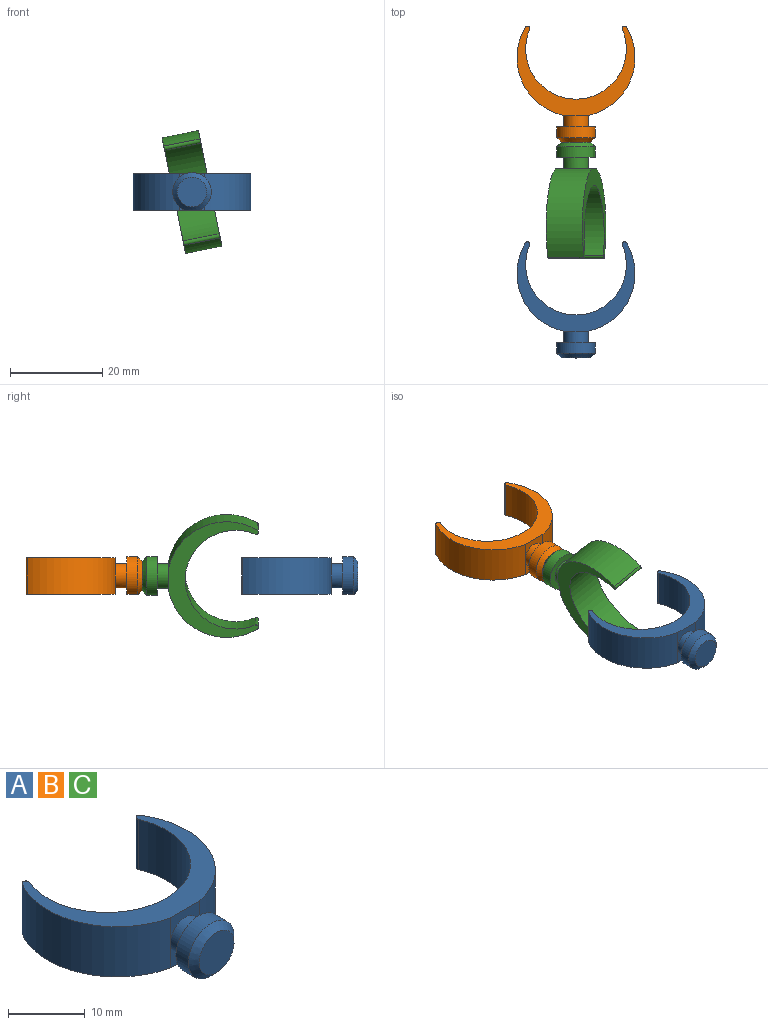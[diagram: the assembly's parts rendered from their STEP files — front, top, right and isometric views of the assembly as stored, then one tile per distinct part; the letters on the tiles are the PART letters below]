
ASSEMBLY  parts=3 mates=2
PART A: 15 faces, bbox 25.5x25.1x8.4 mm
  f0: cylinder r=2.7mm len=5.4mm, axis (0,1,0), area 42.4mm2, adj f1,f5,f6
  f1: plane 8.4x8.2mm, normal (0,1,0), area 32.2mm2, adj f0,f2,f12
  f2: cylinder r=4.2mm len=8.4mm, axis (0,1,0), area 54.7mm2, adj f1,f4,f12
  f3: plane 6.4x6.4mm, normal (0,-1,0), area 32.2mm2, adj f4
  f4: cone r=4.2mm half-angle=45deg, axis (0,1,0), area 32.4mm2, adj f2,f3,f12
  f5: plane 5.4x4mm, normal (0,-1,0), area 10.1mm2, adj f0,f8,f9,f11
  f6: plane 5.4x4mm, normal (0,-1,0), area 10.1mm2, adj f0,f8,f9,f10
  f7: cylinder r=10.9mm len=21.8mm, axis (0,0,-1), area 343.6mm2, adj f10,f11,f13,f14
  f8: cylinder r=12.77mm len=19.09mm, axis (0,0,-1), area 194.3mm2, adj f5,f6,f10,f11,f13
  f9: cylinder r=12.77mm len=19.09mm, axis (0,0,-1), area 194.3mm2, adj f5,f6,f10,f11,f14
  f10: plane 25.55x19.33mm, normal (0,0,1), area 130.7mm2, adj f6,f7,f8,f9,f13,f14
  f11: plane 25.55x19.33mm, normal (0,0,-1), area 130.7mm2, adj f5,f7,f8,f9,f13,f14
  f12: plane 2.57x2.5mm, normal (0,0,-1), area 6.2mm2, adj f1,f2,f4
  f13: cylinder r=0.5mm len=8mm, axis (0,0,1), area 12mm2, adj f7,f8,f10,f11
  f14: cylinder r=0.5mm len=8mm, axis (0,0,1), area 12mm2, adj f7,f9,f10,f11
PART B: same geometry as A
PART C: same geometry as A
PLACE A t=(14.93,-63.58,30.43)mm
PLACE B t=(14.93,-16.88,30.43)mm fixed
PLACE C rot(axis=(0.77,0,-0.63),180deg) t=(14.93,-28.48,30.43)mm
MATE revolute B.f0 <-> C.f0  axis (0,-1,0) through (14.93,-22.68,30.43)mm
MATE slider A.f0 <-> B.f0  axis (0,-1,0) through (14.93,-69.38,30.43)mm
